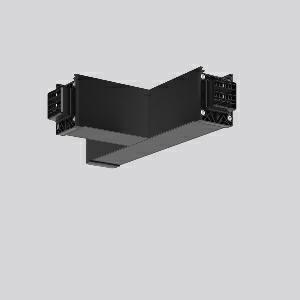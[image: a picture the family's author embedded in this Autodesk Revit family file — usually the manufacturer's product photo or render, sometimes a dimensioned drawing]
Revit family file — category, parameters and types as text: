
# Revit family: linedo_t-verbindung_982774_003_6_a4a7
name_source: partatom
category: Lighting Fixtures
units: mm (PartAtom-declared; Revit-internal decimal feet)

## family parameters
Cut with Voids When Loaded = No
Host = Face
Light Source = No
Part Type = Normal
Room Calculation Point = No
Round Connector Dimension = Use Diameter
Shared = No

## types (1)
- LINEDO T-Verbindung
    Apparent Load = 0 VA
    Default Elevation = 1800 mm
    Description = Series: LINEDO
T-connector, 7-pole, connection plug / socket - plug. Housing: extruded aluminium profile, powder-coated. Cover made of plastic, surface like housing. LINEDO plug system, plastic, black. Easy connection for rigid or flexible wires. 5 membrane cable entries (2 x M20 and 3 x M25). Suitable for power supply in 7-pole version. Ready prewired. Colour-coded individual cables enable easy electromechanical separation.
Colour: jet black (RAL 9005)
Length: 330 mm
Width: 204 mm
Height: 76 mm
Weight: 940 g
    Height = 76 mm
    Lamp = 0 x
    Length = 331 mm
    Luminous efficacy = 0 lm/W
    Manufacturer = RZB
    ModVariant = No
    Model = 982774.003.6
    Mounting Place = Ceiling
    Mounting Type = Surface mounted
    Number of Poles = 1
    OnlyDefault = Yes
    Power Factor = 1
    Product Name = LINEDO T-Verbindung
    Product group = Surface mounted continuous line luminaire system
    ProductGroupID = 310
    Protection Class = Protection class I
    Protection Degree = Degree of protection
    RLX_Detail_Level = 1
    RLX_Emergency_Light_Flux = 0 lm
    RLX_Emergency_Type = 0
    RLX_Emergency_Type_DB = No
    RlxData = <blob elided: 20401 chars, md5=e6675c1d>
    Standby Power = 0 W
    System Light Flux = 0 lm
    System Power = 0 W
    Type Comments = Product without accessories
    Type Image = 982774.003.2.jpg
    URL = http://relux.com
    VarID = ---
    Voltage = 0 V
    Weight = 0.00 kg
    Width = 204 mm

## geometry (parser evidence)
native form markers: Blend x4, Sweep x10
no freeform markers — native parametric forms only
